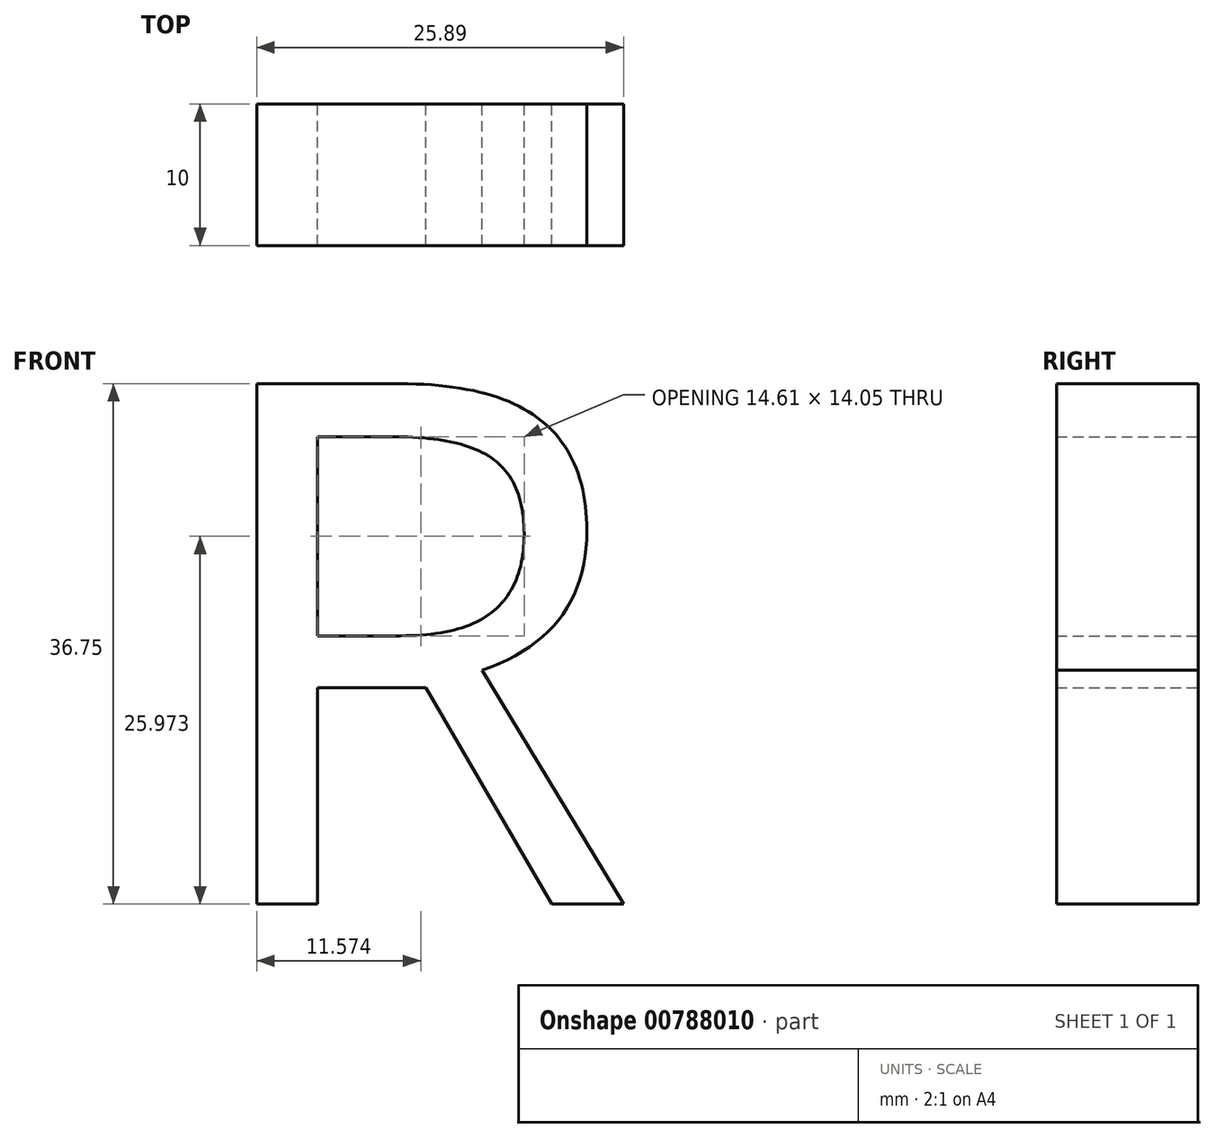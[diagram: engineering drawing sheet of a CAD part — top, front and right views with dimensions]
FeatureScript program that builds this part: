
annotation { "Feature Type Name" : "Feature", "Feature Type Description" : "" }
export const myFeature = defineFeature(function(context is Context, id is Id, definition is map)
    precondition{}
    {
        {
            var Q0;
            Q0=qCreatedBy(makeId("Front.planeOp"),FACE);
            var sketch = newSketch(context, id + "F0", { "sketchPlane" : qUnion([Q0])});
            skText(sketch, "E0", { "text": "R", "fontName": "OpenSans-Regular.ttf"});
            const initialGuessF0  = {"E0": [-0.03427, 0, 1, 0, 0.03706]};
            skSetInitialGuess(sketch, initialGuessF0);
            skSolve(sketch);
        }
        {
            var Q0;
            Q0 = qSketchRegion(id + "F0", true);
            extrude(context, id + "F1", {"entities" : qUnion([Q0]), "depth" : 10 * mm, "offsetDistance" : 25.4 * mm});
        }
    });
